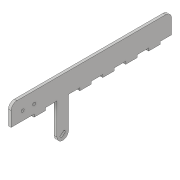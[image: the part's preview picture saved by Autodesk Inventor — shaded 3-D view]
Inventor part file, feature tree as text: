
AUTODESK INVENTOR PART (.ipt)
format: ipt  version: 2017 (Build 210142000, 142)  size: 172,544 bytes
history: native  units: in
note: dims shown in document units (in); Inventor stores cm internally (conversion verified against a paired STEP export)
features: extrude x6, sketch x6, fillet x2, projected_geometry x1
ambient origin geometry x8: Origin, YZ Plane, XZ Plane, XY Plane, X Axis, Y Axis, Z Axis, Center Point
bodies: Solid1 (feature_tree)
feature tree (15):
  extrude  "Extrusion1"  Depth=1.0in
  extrude  "Extrusion2"  Depth=0.115in TaperAngle=0.0deg
  extrude  "Extrusion3"  Depth=0.115in
  extrude  "Extrusion4"  Depth=1.0in
  fillet  "Fillet1"  Radius=0.115in
  extrude  "Extrusion5"  Depth=1.5in TaperAngle=0.0deg
  extrude  "Extrusion6"  Depth=0.25in
  fillet  "Fillet2"  Radius=0.115in
  sketch  "Sketch1"  dims[d0=7.0in d1=1.0in]
  sketch  "Sketch2"  dims[d2=0.0in d3=0.115in d4=0.0in]
  sketch  "Sketch3"  dims[d5=0.5in d6=0.115in]
  sketch  "Sketch4"  dims[d7=0.5in d8=2.7559in d10=1.0in d11=0.3937in d13=1.0in d15=0.115in d16=0.0in]
  projected_geometry  "Projected Loop1"
  sketch  "Sketch5"  dims[d17=1.0in d18=0.0in d19=1.5in d20=0.0in]
  sketch  "Sketch6"  dims[d21=0.25in d22=0.25in d23=0.115in d24=0.25in d25=1.375in d27=1.5in d28=0.0in d29=0.2749in d30=0.125in d31=0.125in d32=0.5in d33=0.5in d34=0.5in d35=0.5in d36=1.5in d37=0.0in d38=0.25in]
